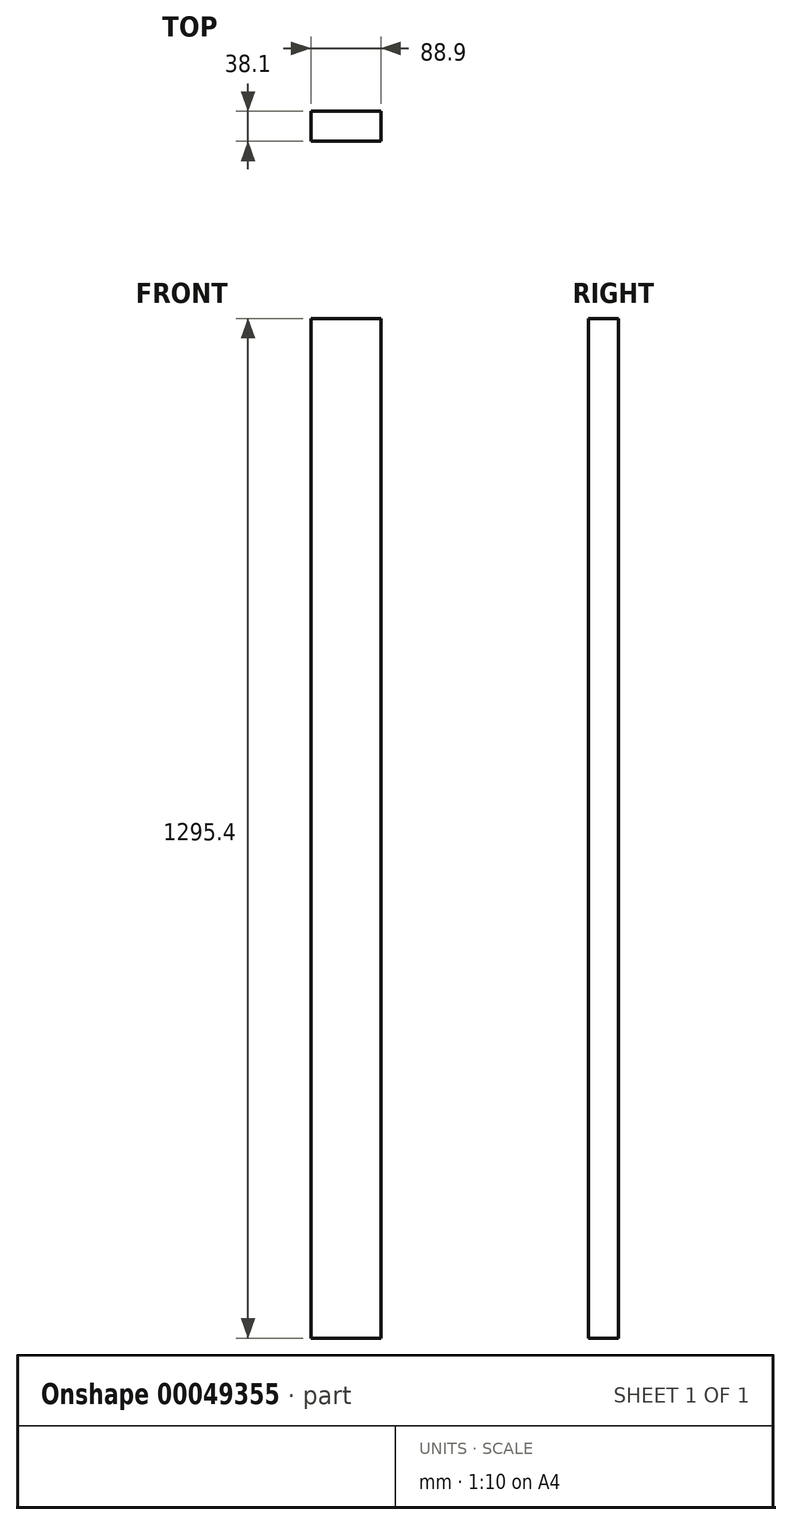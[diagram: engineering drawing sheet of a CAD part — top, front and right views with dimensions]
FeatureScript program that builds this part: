
annotation { "Feature Type Name" : "Feature", "Feature Type Description" : "" }
export const myFeature = defineFeature(function(context is Context, id is Id, definition is map)
    precondition{}
    {
        {
            var Q0;
            Q0=qCreatedBy(makeId("Top.planeOp"),FACE);
            var sketch = newSketch(context, id + "F0", { "sketchPlane" : qUnion([Q0])});
            skLineSegment(sketch, "E0.rect.bottom", {"start": v(44.45, -19.05) * mm, "end": v(-44.45, -19.05) * mm});
            skLineSegment(sketch, "E0.rect.top", {"start": v(44.45, 19.05) * mm, "end": v(-44.45, 19.05) * mm});
            skLineSegment(sketch, "E0.rect.left", {"start": v(44.45, -19.05) * mm, "end": v(44.45, 19.05) * mm});
            skLineSegment(sketch, "E0.rect.right", {"start": v(-44.45, -19.05) * mm, "end": v(-44.45, 19.05) * mm});
            skPoint(sketch, "E0.rect.middle", {"position": v(0, 0) * mm});
            skSolve(sketch);
        }
        {
            var Q0;
            Q0 = qSketchRegion(id + "F0", true);
            extrude(context, id + "F1", {"entities" : qUnion([Q0]), "endBound" : BoundingType.SYMMETRIC, "depth" : 1295.4 * mm});
        }
    });
